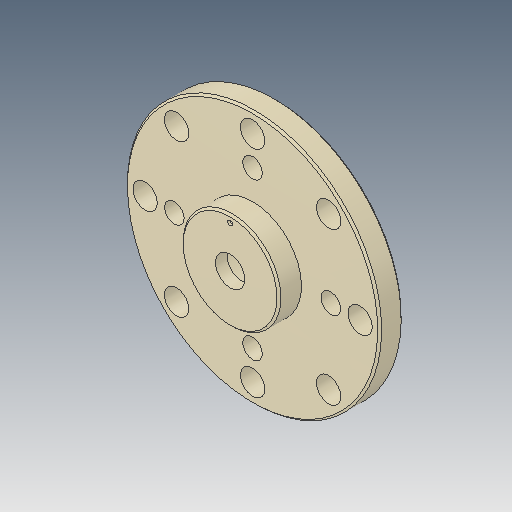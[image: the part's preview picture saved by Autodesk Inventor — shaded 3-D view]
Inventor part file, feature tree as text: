
AUTODESK INVENTOR PART (.ipt)
format: ipt  version: 2019.4 (Build 234330000, 330)  size: 202,240 bytes
history: native  units: mm
features: sketch x4, hole x3, other x1, revolve x1, chamfer x1
ambient origin geometry x8: Origin, YZ Plane, XZ Plane, XY Plane, X Axis, Y Axis, Z Axis, Center Point
bodies: Body1 (feature_tree)
feature tree (10):
  other  "ソリッド1"
  revolve  "回転1"
  hole  "穴1"  [1 undecoded]
  hole  "穴2"  [1 undecoded]
  chamfer  "面取り1"  Distance=5.3mm
  hole  "穴3"  [1 undecoded]
  sketch  "スケッチ1"
  sketch  "スケッチ2"
  sketch  "スケッチ3"
  sketch  "スケッチ4"
note: 3 required parameter values undecoded (feature->parameter linkage not recoverable at this tier; creation-order binding heuristic only, values carry confidence <= 0.55)
